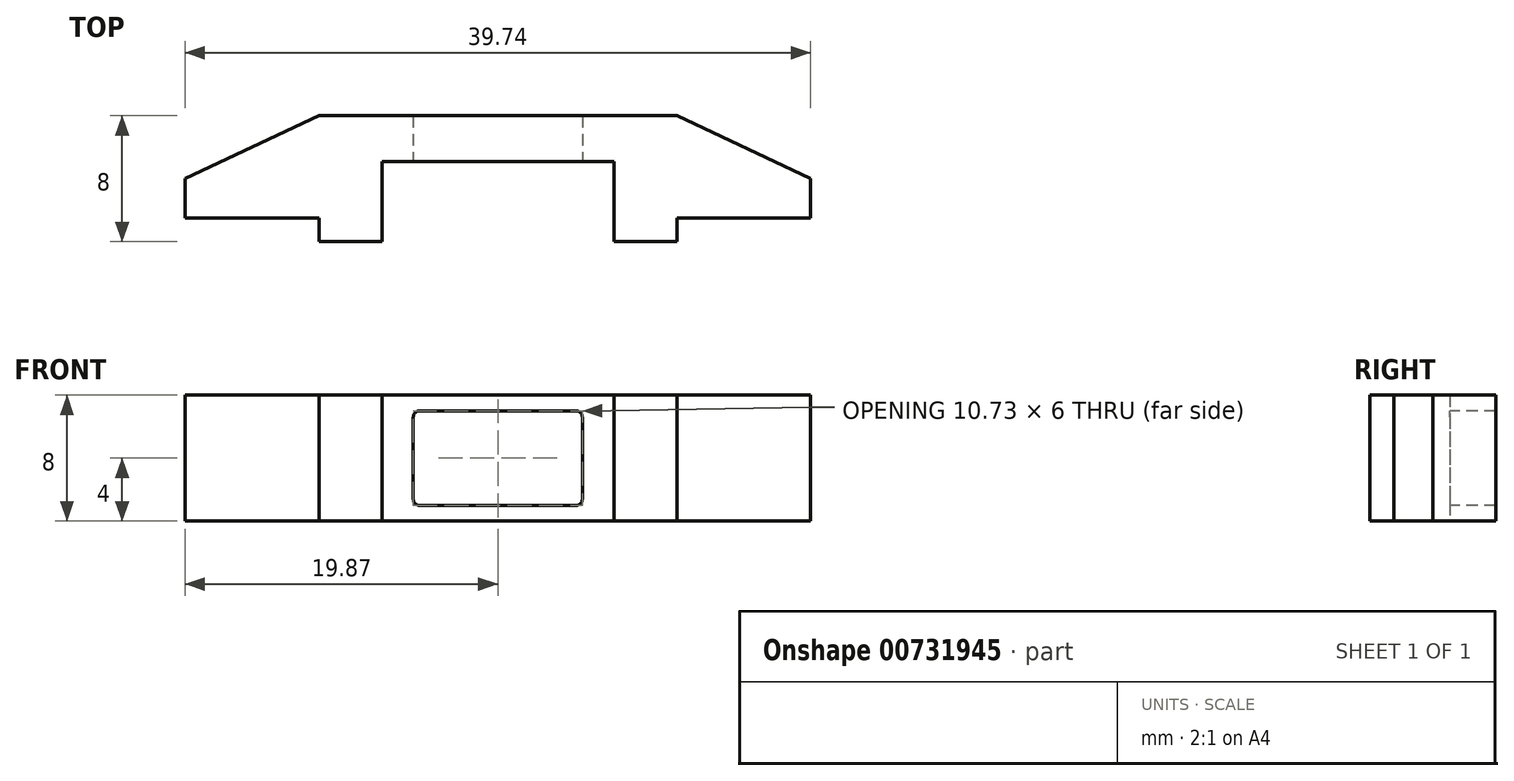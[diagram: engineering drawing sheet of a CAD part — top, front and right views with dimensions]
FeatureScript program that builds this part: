
annotation { "Feature Type Name" : "Feature", "Feature Type Description" : "" }
export const myFeature = defineFeature(function(context is Context, id is Id, definition is map)
    precondition{}
    {
        {
            var Q0;
            Q0=qCreatedBy(makeId("Top.planeOp"),FACE);
            var sketch = newSketch(context, id + "F0", { "sketchPlane" : qUnion([Q0])});
            skLineSegment(sketch, "E0", {"start": v(-11.37, 4) * mm, "end": v(11.37, 4) * mm});
            skLineSegment(sketch, "E1", {"start": v(11.37, 4) * mm, "end": v(11.37, 0) * mm});
            skLineSegment(sketch, "E2", {"start": v(11.37, 0) * mm, "end": v(19.87, 0) * mm});
            skLineSegment(sketch, "E3", {"start": v(19.87, 0) * mm, "end": v(19.87, -4) * mm});
            skLineSegment(sketch, "E4", {"start": v(19.87, -4) * mm, "end": v(7.37, -4) * mm});
            skLineSegment(sketch, "E5", {"start": v(-19.87, -4) * mm, "end": v(-19.87, 0) * mm});
            skLineSegment(sketch, "E6", {"start": v(-19.87, 0) * mm, "end": v(-11.37, 0) * mm});
            skLineSegment(sketch, "E7", {"start": v(-11.37, 0) * mm, "end": v(-11.37, 4) * mm});
            skLineSegment(sketch, "E8.top", {"start": v(-7.37, 1.08) * mm, "end": v(7.37, 1.08) * mm});
            skLineSegment(sketch, "E8.left", {"start": v(-7.37, -4) * mm, "end": v(-7.37, 1.08) * mm});
            skLineSegment(sketch, "E8.right", {"start": v(7.37, -4) * mm, "end": v(7.37, 1.08) * mm});
            skLineSegment(sketch, "E9.trimOffspring", {"start": v(-7.37, -4) * mm, "end": v(-19.87, -4) * mm});
            skPoint(sketch, "E10", {"position": v(0, 1.08) * mm});
            skLineSegment(sketch, "E11.bottom", {"start": v(-19.87, -4) * mm, "end": v(-11.37, -4) * mm});
            skLineSegment(sketch, "E11.top", {"start": v(-19.87, -2.5) * mm, "end": v(-11.37, -2.5) * mm});
            skLineSegment(sketch, "E11.left", {"start": v(-19.87, -4) * mm, "end": v(-19.87, -2.5) * mm});
            skLineSegment(sketch, "E11.right", {"start": v(-11.37, -4) * mm, "end": v(-11.37, -2.5) * mm});
            skLineSegment(sketch, "E12.bottom", {"start": v(19.87, -4) * mm, "end": v(11.37, -4) * mm});
            skLineSegment(sketch, "E12.top", {"start": v(19.87, -2.5) * mm, "end": v(11.37, -2.5) * mm});
            skLineSegment(sketch, "E12.left", {"start": v(19.87, -4) * mm, "end": v(19.87, -2.5) * mm});
            skLineSegment(sketch, "E12.right", {"start": v(11.37, -4) * mm, "end": v(11.37, -2.5) * mm});
            skSolve(sketch);
        }
        {
            var Q0;
            Q0=makeQuery(id+"F0.imprint","IMPRINT",FACE,{"disambiguationData":[TD([[makeQuery(id+"F0.imprint","IMPRINT",EDGE,{"derivedFrom":sQuery(id+"F0.wireOp",EDGE,"E0")}),-1.0]])]});
            extrude(context, id + "F1", {"entities" : qUnion([Q0]), "depth" : 8 * mm, "offsetDistance" : 25 * mm});
        }
        {
            var Q0;
            Q0=makeQuery(id+"F1.opExtrude","SWEPT_FACE",FACE,{"disambiguationData":[OSD([sQuery(id+"F0.wireOp",EDGE,"E8.top")])]});
            var sketch = newSketch(context, id + "F2", { "sketchPlane" : qUnion([Q0])});
            skLineSegment(sketch, "E13.bottom", {"start": v(-5.37, 7) * mm, "end": v(5.37, 7) * mm});
            skLineSegment(sketch, "E13.top", {"start": v(-5.37, 1) * mm, "end": v(5.37, 1) * mm});
            skLineSegment(sketch, "E13.left", {"start": v(-5.37, 7) * mm, "end": v(-5.37, 1) * mm});
            skLineSegment(sketch, "E13.right", {"start": v(5.37, 7) * mm, "end": v(5.37, 1) * mm});
            skPoint(sketch, "E14", {"position": v(0, 7) * mm});
            skPoint(sketch, "E15", {"position": v(0, 8) * mm});
            skSolve(sketch);
        }
        {
            var Q0;
            Q0 = qSketchRegion(id + "F2", true);
            extrude(context, id + "F3", {"entities" : qUnion([Q0]), "operationType" : NewBodyOperationType.REMOVE, "oppositeDirection" : true, "depth" : 25 * mm, "offsetDistance" : 25 * mm});
        }
        {
            var Q0;
            Q0=makeQuery(id+"F3.boolean.opBoolean","COPY",EDGE,{"derivedFrom":makeQuery(id+"F3.opExtrude","SWEPT_EDGE",EDGE,{"disambiguationData":[OSD([sQuery(id+"F2.wireOp",EDGE,"E13.top"),sQuery(id+"F2.wireOp",EDGE,"E13.left")])]})});
            var Q1;
            Q1=makeQuery(id+"F3.boolean.opBoolean","COPY",EDGE,{"derivedFrom":makeQuery(id+"F3.opExtrude","SWEPT_EDGE",EDGE,{"disambiguationData":[OSD([sQuery(id+"F2.wireOp",EDGE,"E13.bottom"),sQuery(id+"F2.wireOp",EDGE,"E13.left")])]})});
            var Q2;
            Q2=makeQuery(id+"F3.boolean.opBoolean","COPY",EDGE,{"derivedFrom":makeQuery(id+"F3.opExtrude","SWEPT_EDGE",EDGE,{"disambiguationData":[OSD([sQuery(id+"F2.wireOp",EDGE,"E13.bottom"),sQuery(id+"F2.wireOp",EDGE,"E13.right")])]})});
            var Q3;
            Q3=makeQuery(id+"F3.boolean.opBoolean","COPY",EDGE,{"derivedFrom":makeQuery(id+"F3.opExtrude","SWEPT_EDGE",EDGE,{"disambiguationData":[OSD([sQuery(id+"F2.wireOp",EDGE,"E13.top"),sQuery(id+"F2.wireOp",EDGE,"E13.right")])]})});
            fillet(context, id + "F4", {"entities" : qUnion([Q0, Q1, Q2, Q3]), "radius" : 0.39 * mm, "tangentPropagation" : true, "allowEdgeOverflow" : false});
        }
        {
            var Q0;
            Q0=makeQuery(id+"F1.opExtrude","CAP_FACE",FACE,{"disambiguationData":[OSD([sQuery(id+"F0.wireOp",EDGE,"E0"),sQuery(id+"F0.wireOp",EDGE,"E1"),sQuery(id+"F0.wireOp",EDGE,"E2"),sQuery(id+"F0.wireOp",EDGE,"E3"),sQuery(id+"F0.wireOp",EDGE,"E4"),sQuery(id+"F0.wireOp",EDGE,"E5"),sQuery(id+"F0.wireOp",EDGE,"E6"),sQuery(id+"F0.wireOp",EDGE,"E7"),sQuery(id+"F0.wireOp",EDGE,"E8.top"),sQuery(id+"F0.wireOp",EDGE,"E8.left"),sQuery(id+"F0.wireOp",EDGE,"E8.right"),sQuery(id+"F0.wireOp",EDGE,"E9.trimOffspring"),sQuery(id+"F0.wireOp",EDGE,"E11.top"),sQuery(id+"F0.wireOp",EDGE,"E11.right"),sQuery(id+"F0.wireOp",EDGE,"E12.top"),sQuery(id+"F0.wireOp",EDGE,"E12.right")])],"isStart":false});
            var sketch = newSketch(context, id + "F5", { "sketchPlane" : qUnion([Q0])});
            skLineSegment(sketch, "E16", {"start": v(11.37, 4) * mm, "end": v(19.87, 0) * mm});
            skLineSegment(sketch, "E17", {"start": v(19.87, 0) * mm, "end": v(11.37, 0) * mm});
            skLineSegment(sketch, "E18", {"start": v(11.37, 0) * mm, "end": v(11.37, 4) * mm});
            skLineSegment(sketch, "E19", {"start": v(0, 9.92) * mm, "end": v(0, -4.95) * mm});
            skLineSegment(sketch, "E20.MirrorCS", {"start": v(-11.37, 4) * mm, "end": v(-19.87, 0) * mm});
            skLineSegment(sketch, "E21.MirrorCS", {"start": v(-11.37, 0) * mm, "end": v(-11.37, 4) * mm});
            skLineSegment(sketch, "E22.MirrorCS", {"start": v(-19.87, 0) * mm, "end": v(-11.37, 0) * mm});
            skSolve(sketch);
        }
        {
            var Q0;
            Q0 = qSketchRegion(id + "F5", true);
            extrude(context, id + "F6", {"entities" : qUnion([Q0]), "operationType" : NewBodyOperationType.ADD, "oppositeDirection" : true, "depth" : 8 * mm, "offsetDistance" : 25 * mm});
        }
    });
